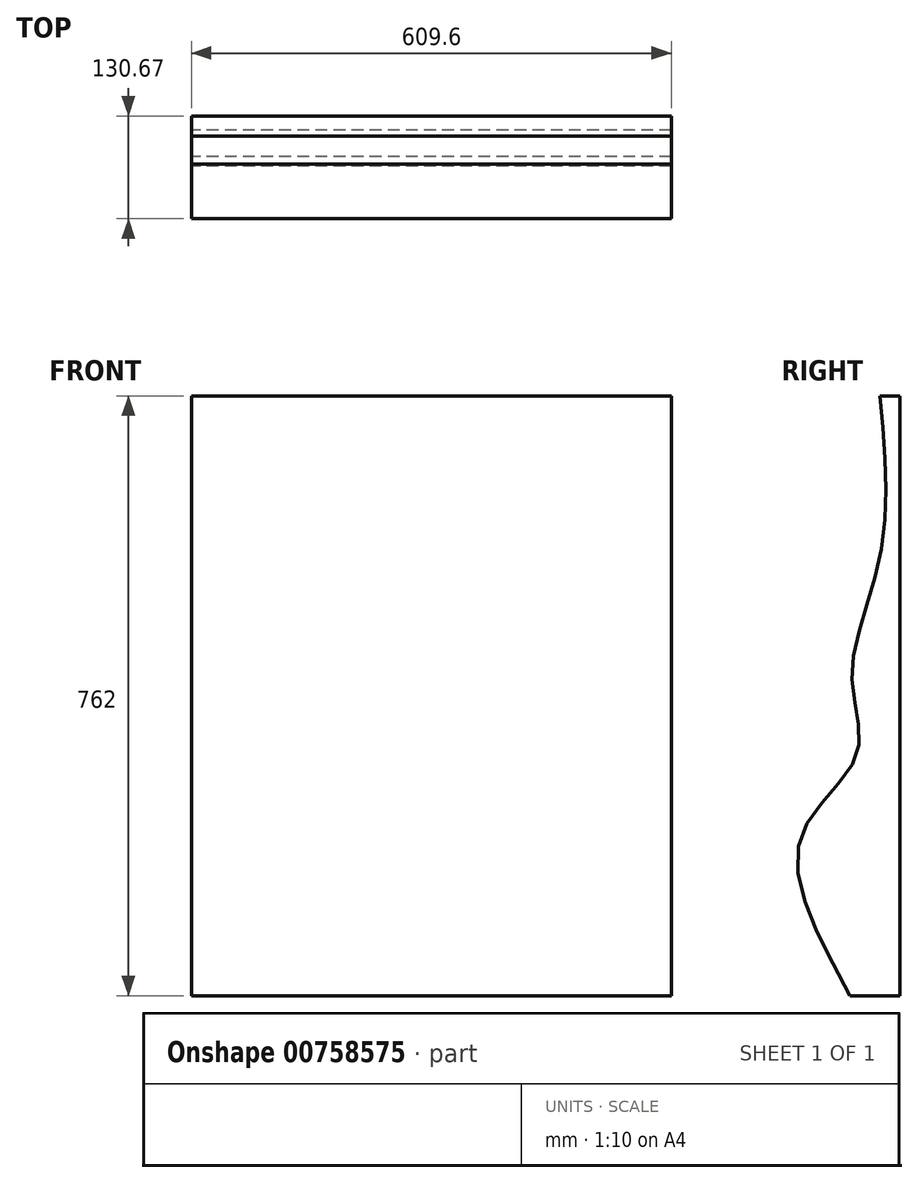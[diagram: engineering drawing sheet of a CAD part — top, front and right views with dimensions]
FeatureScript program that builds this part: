
annotation { "Feature Type Name" : "Feature", "Feature Type Description" : "" }
export const myFeature = defineFeature(function(context is Context, id is Id, definition is map)
    precondition{}
    {
        {
            var Q0;
            Q0=qCreatedBy(makeId("Front.planeOp"),FACE);
            var sketch = newSketch(context, id + "F0", { "sketchPlane" : qUnion([Q0])});
            skLineSegment(sketch, "E0.bottom", {"start": v(304.8, -381) * mm, "end": v(-304.8, -381) * mm});
            skLineSegment(sketch, "E0.top", {"start": v(304.8, 381) * mm, "end": v(-304.8, 381) * mm});
            skLineSegment(sketch, "E0.left", {"start": v(304.8, -381) * mm, "end": v(304.8, 381) * mm});
            skLineSegment(sketch, "E0.right", {"start": v(-304.8, -381) * mm, "end": v(-304.8, 381) * mm});
            skPoint(sketch, "E0.middle", {"position": v(0, 0) * mm});
            skSolve(sketch);
        }
        {
            var Q0;
            Q0=makeQuery(id+"F0.imprint","IMPRINT",FACE,{"disambiguationData":[TD([[makeQuery(id+"F0.imprint","IMPRINT",EDGE,{"derivedFrom":sQuery(id+"F0.wireOp",EDGE,"E0.bottom")}),-1.0]])]});
            extrude(context, id + "F1", {"entities" : qUnion([Q0]), "depth" : 228.6 * mm, "offsetDistance" : 25.4 * mm});
        }
        {
            var Q0;
            Q0=makeQuery(id+"F1.opExtrude","SWEPT_FACE",FACE,{"disambiguationData":[OSD([sQuery(id+"F0.wireOp",EDGE,"E0.right")])]});
            var sketch = newSketch(context, id + "F2", { "sketchPlane" : qUnion([Q0])});
            skLineSegment(sketch, "E1", {"start": v(63.5, 381) * mm, "end": v(63.5, -381) * mm, "construction": true});
            skPoint(sketch, "E1.startSnap0", {"position": v(114.3, 381) * mm});
            skLineSegment(sketch, "E2", {"start": v(114.3, 381) * mm, "end": v(114.3, 381) * mm});
            skLineSegment(sketch, "E3", {"start": v(127, 381) * mm, "end": v(127, -381) * mm, "construction": true});
            skLineSegment(sketch, "E4", {"start": v(25.4, 381) * mm, "end": v(25.4, -381) * mm, "construction": true});
            skLineSegment(sketch, "E5", {"start": v(0, 177.8) * mm, "end": v(228.6, 177.8) * mm, "construction": true});
            skLineSegment(sketch, "E6", {"start": v(0, 25.4) * mm, "end": v(228.6, 25.4) * mm, "construction": true});
            skLineSegment(sketch, "E7", {"start": v(0, -76.2) * mm, "end": v(228.6, -76.2) * mm, "construction": true});
            skLineSegment(sketch, "E8", {"start": v(0, -228.6) * mm, "end": v(228.6, -228.6) * mm, "construction": true});
            skFitSpline(sketch, "E9", {"points": [v(25.4, 381) * mm, v(25.4, 177.8) * mm, v(61.34, 25.4) * mm, v(55.4, -76.2) * mm, v(127, -182) * mm, v(63.5, -381) * mm], "startDerivative": vector(-81.75, -920.81) * mm, "endDerivative": vector(-517.35, -946.26) * mm});
            skSolve(sketch);
        }
        {
            var Q0;
            {var subQ0=sQuery(id+"F2.wireOp",EDGE,"E9");Q0=makeQuery(id+"F2.imprint","IMPRINT",FACE,{"disambiguationData":[TD([[makeQuery(id+"F2.imprint","IMPRINT",EDGE,{"derivedFrom":subQ0}),1.0]])]});}
            extrude(context, id + "F3", {"entities" : qUnion([Q0]), "operationType" : NewBodyOperationType.REMOVE, "oppositeDirection" : true, "depth" : 609.6 * mm, "offsetDistance" : 25.4 * mm});
        }
    });
